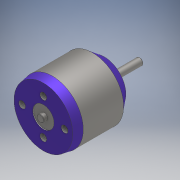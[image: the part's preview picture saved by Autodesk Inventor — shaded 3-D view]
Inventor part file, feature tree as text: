
AUTODESK INVENTOR PART (.ipt)
format: ipt  version: 2017 (Build 210142000, 142)  size: 202,240 bytes
history: native  units: mm
features: sketch x8, extrude x7, thread x5, chamfer x2, revolve x1, pattern_circular x1
ambient origin geometry x8: Origin, YZ Plane, XZ Plane, XY Plane, X Axis, Y Axis, Z Axis, Center Point
bodies: Solid1 (feature_tree)
feature tree (24):
  extrude  "Extrusion1"  Depth=22.0mm TaperAngle=0.0deg
  revolve  "Revolution1"  Angle=90.0deg
  chamfer  "Chamfer1"  Distance=2.0mm
  extrude  "Extrusion2"  Depth=15.82mm TaperAngle=0.0deg
  extrude  "Extrusion3"  Depth=2.0mm TaperAngle=0.0deg
  extrude  "Extrusion4"  Depth=2.0mm
  thread  "Thread1"  [1 undecoded]
  pattern_circular  "Circular Pattern1"  Count=4 Angle=360.0deg
  extrude  "Extrusion5"  Depth=8.0mm
  thread  "Thread2"  [1 undecoded]
  thread  "Thread3"  [1 undecoded]
  thread  "Thread4"  [1 undecoded]
  thread  "Thread5"  [1 undecoded]
  extrude  "Extrusion6"  Depth=10.0mm TaperAngle=0.0deg
  extrude  "Extrusion7"  Depth=10.0mm TaperAngle=0.0deg
  chamfer  "Chamfer2"  Distance=9.5mm
  sketch  "Sketch1"  dims[d0=27.7mm d1=22.0mm d2=0.0mm]
  sketch  "Sketch2"  dims[d3=5.25mm d5=90.0deg]
  sketch  "Sketch3"  dims[d6=9.65mm d7=4.0mm d8=2.0mm d9=1.745329mm]
  sketch  "Sketch4"  dims[d10=3.16mm d11=15.82mm d12=0.0mm]
  sketch  "Sketch5"  dims[d13=8.97mm d14=2.0mm d15=0.0mm]
  sketch  "Sketch6"  dims[d16=6.0mm d17=2.0mm d18=3.0mm d19=0.0mm]
  sketch  "Sketch7"  dims[d20=10.0mm d21=0.0mm d22=40.0mm d23=360.0deg]
  sketch  "Sketch8"  dims[d25=9.5mm d26=8.0mm d27=3.0mm d28=5.0mm d29=0.0mm d30=10.0mm d31=0.0mm d32=10.0mm d33=0.0mm d34=10.0mm d35=0.0mm d36=10.0mm d37=0.0mm d38=9.5mm d39=0.3mm d40=0.0mm d41=1.7mm d42=0.0mm d43=0.2mm d44=2.0mm d45=45.0deg]
note: 5 required parameter values undecoded (feature->parameter linkage not recoverable at this tier; creation-order binding heuristic only, values carry confidence <= 0.55)
